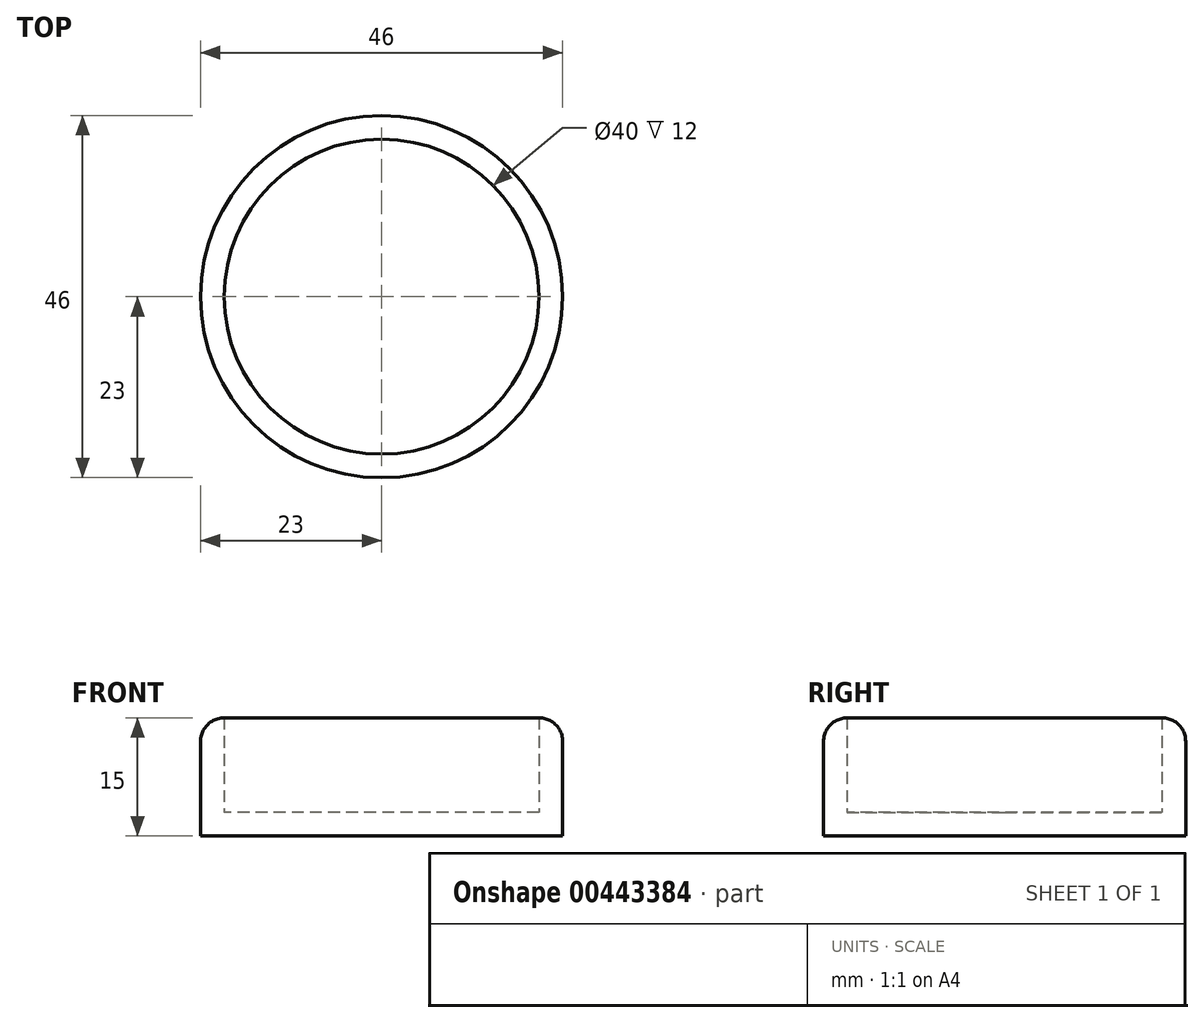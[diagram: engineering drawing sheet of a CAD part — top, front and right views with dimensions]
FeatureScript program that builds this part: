
annotation { "Feature Type Name" : "Feature", "Feature Type Description" : "" }
export const myFeature = defineFeature(function(context is Context, id is Id, definition is map)
    precondition{}
    {
        {
            var Q0;
            Q0=qCreatedBy(makeId("Top.planeOp"),FACE);
            var sketch = newSketch(context, id + "F0", { "sketchPlane" : qUnion([Q0])});
            skCircle(sketch, "E0", {"center": v(0, 0) * mm, "radius": 23 * mm});
            skCircle(sketch, "E1", {"center": v(0, 0) * mm, "radius": 20 * mm});
            skSolve(sketch);
        }
        {
            var Q0;
            Q0=makeQuery(id+"F0.imprint","IMPRINT",FACE,{"disambiguationData":[TD([[makeQuery(id+"F0.imprint","IMPRINT",EDGE,{"derivedFrom":sQuery(id+"F0.wireOp",EDGE,"E0")}),1.0]])]});
            extrude(context, id + "F1", {"entities" : qUnion([Q0]), "depth" : 15 * mm});
        }
        {
            var Q0;
            Q0=qCreatedBy(makeId("Top.planeOp"),FACE);
            var sketch = newSketch(context, id + "F2", { "sketchPlane" : qUnion([Q0])});
            skCircle(sketch, "E2", {"center": v(0, 0) * mm, "radius": 23 * mm});
            skSolve(sketch);
        }
        {
            var Q0;
            Q0=makeQuery(id+"F2.imprint","IMPRINT",FACE,{"disambiguationData":[TD([[makeQuery(id+"F2.imprint","IMPRINT",EDGE,{"derivedFrom":sQuery(id+"F2.wireOp",EDGE,"E2")}),1.0]])]});
            extrude(context, id + "F3", {"entities" : qUnion([Q0]), "operationType" : NewBodyOperationType.ADD, "depth" : 3 * mm});
        }
        {
            var Q0;
            Q0=makeQuery(id+"F1.opExtrude","CAP_EDGE",EDGE,{"disambiguationData":[OSD([sQuery(id+"F0.wireOp",EDGE,"E0")])],"isStart":false});
            fillet(context, id + "F4", {"entities" : qUnion([Q0]), "radius" : 3 * mm, "tangentPropagation" : true, "allowEdgeOverflow" : false});
        }
    });
